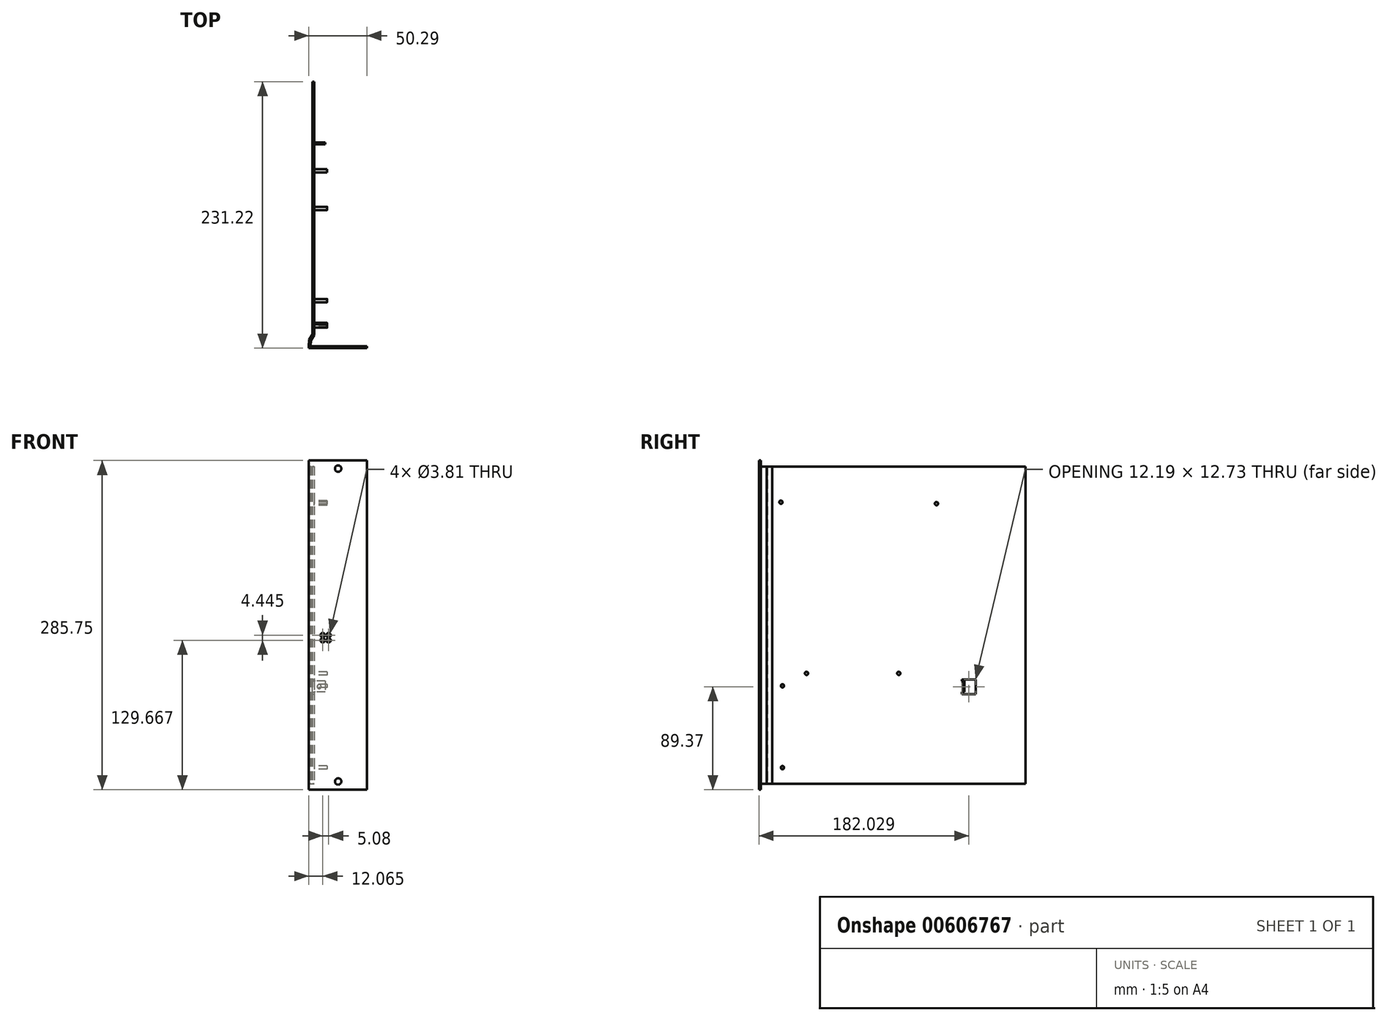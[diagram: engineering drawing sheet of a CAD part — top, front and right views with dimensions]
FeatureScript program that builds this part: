
annotation { "Feature Type Name" : "Feature", "Feature Type Description" : "" }
export const myFeature = defineFeature(function(context is Context, id is Id, definition is map)
    precondition{}
    {
        {
            var Q0;
            Q0=qCreatedBy(makeId("Top.planeOp"),FACE);
            var sketch = newSketch(context, id + "F0", { "sketchPlane" : qUnion([Q0])});
            skLineSegment(sketch, "E0", {"start": v(0, 0) * mm, "end": v(50.3, 0) * mm});
            skLineSegment(sketch, "E1", {"start": v(0, 0) * mm, "end": v(0, 1.6) * mm});
            skLineSegment(sketch, "E2.0", {"start": v(3.15, 231.22) * mm, "end": v(4.75, 231.22) * mm});
            skLineSegment(sketch, "E3.0", {"start": v(3.15, 11.84) * mm, "end": v(3.15, 231.22) * mm});
            skLineSegment(sketch, "E4.0", {"start": v(4.75, 11.38) * mm, "end": v(4.75, 231.22) * mm});
            skLineSegment(sketch, "E5.0", {"start": v(1.6, 1.6) * mm, "end": v(50.3, 1.6) * mm});
            skLineSegment(sketch, "E6", {"start": v(0, 1.6) * mm, "end": v(0.3, 7.25) * mm});
            skLineSegment(sketch, "E7", {"start": v(3.15, 11.84) * mm, "end": v(0.3, 7.25) * mm});
            skLineSegment(sketch, "E8.0", {"start": v(4.75, 11.38) * mm, "end": v(1.87, 6.76) * mm});
            skLineSegment(sketch, "E9.0", {"start": v(1.6, 1.6) * mm, "end": v(1.87, 6.76) * mm});
            skLineSegment(sketch, "E10", {"start": v(50.3, 1.6) * mm, "end": v(50.3, 0) * mm});
            skSolve(sketch);
        }
        {
            var Q0;
            Q0=qSketchRegion(id+"F0",true);
            extrude(context, id + "F1", {"entities" : qUnion([Q0]), "depth" : 285.75 * mm, "offsetDistance" : 25.4 * mm});
        }
        {
            var Q0;
            Q0=qCreatedBy(makeId("Right.planeOp"),FACE);
            var sketch = newSketch(context, id + "F2", { "sketchPlane" : qUnion([Q0])});
            skLineSegment(sketch, "E11.bottom", {"start": v(231.22, 0) * mm, "end": v(1.6, 0) * mm});
            skLineSegment(sketch, "E11.top", {"start": v(231.22, 5.08) * mm, "end": v(1.6, 5.08) * mm});
            skLineSegment(sketch, "E11.left", {"start": v(231.22, 0) * mm, "end": v(231.22, 5.08) * mm});
            skLineSegment(sketch, "E11.right", {"start": v(1.6, 0) * mm, "end": v(1.6, 5.08) * mm});
            skSolve(sketch);
        }
        {
            var Q0;
            Q0=makeQuery(id+"F2.imprint","IMPRINT",FACE,{"disambiguationData":[TD([[makeQuery(id+"F2.imprint","IMPRINT",EDGE,{"derivedFrom":sQuery(id+"F2.wireOp",EDGE,"E11.bottom")}),-1.0]])]});
            extrude(context, id + "F3", {"entities" : qUnion([Q0]), "operationType" : NewBodyOperationType.REMOVE, "depth" : 6.35 * mm, "offsetDistance" : 25.4 * mm});
        }
        {
            var Q0;
            Q0=qCreatedBy(makeId("Right.planeOp"),FACE);
            var sketch = newSketch(context, id + "F4", { "sketchPlane" : qUnion([Q0])});
            skLineSegment(sketch, "E12.bottom", {"start": v(231.22, 285.75) * mm, "end": v(1.6, 285.75) * mm});
            skLineSegment(sketch, "E12.top", {"start": v(231.22, 280.42) * mm, "end": v(1.6, 280.42) * mm});
            skLineSegment(sketch, "E12.left", {"start": v(231.22, 285.75) * mm, "end": v(231.22, 280.42) * mm});
            skLineSegment(sketch, "E12.right", {"start": v(1.6, 285.75) * mm, "end": v(1.6, 280.42) * mm});
            skSolve(sketch);
        }
        {
            var Q0;
            Q0=qSketchRegion(id+"F4",true);
            extrude(context, id + "F5", {"entities" : qUnion([Q0]), "operationType" : NewBodyOperationType.REMOVE, "depth" : 6.35 * mm, "offsetDistance" : 25.4 * mm});
        }
        {
            var Q0;
            Q0=makeQuery(id+"F1.opExtrude","SWEPT_FACE",FACE,{"disambiguationData":[OSD([sQuery(id+"F0.wireOp",EDGE,"E4.0")])]});
            var sketch = newSketch(context, id + "F6", { "sketchPlane" : qUnion([Q0])});
            skCircle(sketch, "E13", {"center": v(154, 248.28) * mm, "radius": 1.42 * mm});
            skCircle(sketch, "E14", {"center": v(19.13, 249.55) * mm, "radius": 1.42 * mm});
            skCircle(sketch, "E15", {"center": v(121.28, 100.96) * mm, "radius": 1.42 * mm});
            skCircle(sketch, "E16", {"center": v(20.42, 90.14) * mm, "radius": 1.42 * mm});
            skPoint(sketch, "E17", {"position": v(41.28, 100.96) * mm});
            skCircle(sketch, "E18", {"center": v(41.28, 100.96) * mm, "radius": 1.42 * mm});
            skPoint(sketch, "E19", {"position": v(20.42, 19.15) * mm});
            skCircle(sketch, "E20", {"center": v(20.42, 19.15) * mm, "radius": 1.42 * mm});
            skSolve(sketch);
        }
        {
            var Q0;
            Q0=qSketchRegion(id+"F6",true);
            extrude(context, id + "F7", {"entities" : qUnion([Q0]), "operationType" : NewBodyOperationType.ADD, "depth" : 11.1 * mm, "offsetDistance" : 25.4 * mm});
        }
        {
            var Q0;
            Q0=makeQuery(id+"F1.opExtrude","SWEPT_FACE",FACE,{"disambiguationData":[OSD([sQuery(id+"F0.wireOp",EDGE,"E4.0")])]});
            var sketch = newSketch(context, id + "F8", { "sketchPlane" : qUnion([Q0])});
            skLineSegment(sketch, "E21.bottom", {"start": v(175.93, 95.73) * mm, "end": v(188.13, 95.73) * mm});
            skLineSegment(sketch, "E21.top", {"start": v(175.93, 83) * mm, "end": v(188.13, 83) * mm});
            skLineSegment(sketch, "E21.left", {"start": v(175.93, 95.73) * mm, "end": v(175.93, 83) * mm});
            skLineSegment(sketch, "E21.right", {"start": v(188.13, 95.73) * mm, "end": v(188.13, 83) * mm});
            skSolve(sketch);
        }
        {
            var Q0;
            Q0=makeQuery(id+"F8.imprint","IMPRINT",FACE,{"disambiguationData":[TD([[makeQuery(id+"F8.imprint","IMPRINT",EDGE,{"derivedFrom":sQuery(id+"F8.wireOp",EDGE,"E21.bottom")}),-1.0]])]});
            extrude(context, id + "F9", {"entities" : qUnion([Q0]), "operationType" : NewBodyOperationType.REMOVE, "oppositeDirection" : true, "depth" : 25.4 * mm, "offsetDistance" : 25.4 * mm});
        }
        {
            var Q0;
            Q0=qCreatedBy(makeId("Top.planeOp"),FACE);
            cPlane(context, id + "F10", {"entities" : qUnion([Q0]), "cplaneType" : CPlaneType.OFFSET, "offset" : 84.73 * mm, "width" : 152.4 * mm, "height" : 152.4 * mm});
        }
        {
            var Q0;
            Q0=qCreatedBy(id+"F10.planeOp",FACE);
            var sketch = newSketch(context, id + "F11", { "sketchPlane" : qUnion([Q0])});
            skLineSegment(sketch, "E22.0", {"start": v(14.27, 178.33) * mm, "end": v(14.27, 176.73) * mm});
            skLineSegment(sketch, "E23", {"start": v(14.27, 176.73) * mm, "end": v(5.55, 176.73) * mm});
            skLineSegment(sketch, "E24.0", {"start": v(14.27, 178.33) * mm, "end": v(4.75, 178.33) * mm});
            skArc(sketch, "E25", {"start": v(5.55, 176.73) * mm, "mid": v(4.98, 176.5) * mm, "end": v(4.75, 175.93) * mm});
            skLineSegment(sketch, "E26", {"start": v(3.15, 175.93) * mm, "end": v(3.15, 176.73) * mm});
            skArc(sketch, "E27", {"start": v(4.75, 178.33) * mm, "mid": v(3.62, 177.86) * mm, "end": v(3.15, 176.73) * mm});
            skLineSegment(sketch, "E28.0", {"start": v(3.15, 175.93) * mm, "end": v(4.75, 175.93) * mm});
            skSolve(sketch);
        }
        {
            var Q0;
            Q0=makeQuery(id+"F11.imprint","IMPRINT",FACE,{"disambiguationData":[TD([[makeQuery(id+"F11.imprint","IMPRINT",EDGE,{"derivedFrom":sQuery(id+"F11.wireOp",EDGE,"E22.0")}),-1.0]])]});
            extrude(context, id + "F12", {"entities" : qUnion([Q0]), "operationType" : NewBodyOperationType.ADD, "depth" : 9.52 * mm, "offsetDistance" : 25.4 * mm});
        }
        {
            var Q0;
            Q0=makeQuery(id+"F12.opExtrude","SWEPT_FACE",FACE,{"disambiguationData":[OSD([sQuery(id+"F11.wireOp",EDGE,"E24.0")])]});
            var sketch = newSketch(context, id + "F13", { "sketchPlane" : qUnion([Q0])});
            skCircle(sketch, "E29", {"center": v(-9, 89.5) * mm, "radius": 1.78 * mm});
            skPoint(sketch, "E29.centerSnap0", {"position": v(-14.27, 89.5) * mm});
            skSolve(sketch);
        }
        {
            var Q0;
            Q0=makeQuery(id+"F13.imprint","IMPRINT",FACE,{"disambiguationData":[TD([[makeQuery(id+"F13.imprint","IMPRINT",EDGE,{"derivedFrom":sQuery(id+"F13.wireOp",EDGE,"E29")}),1.0]])]});
            extrude(context, id + "F14", {"entities" : qUnion([Q0]), "operationType" : NewBodyOperationType.REMOVE, "endBound" : BoundingType.UP_TO_NEXT, "oppositeDirection" : true, "depth" : 25.4 * mm, "offsetDistance" : 25.4 * mm});
        }
        {
            var Q0;
            Q0=makeQuery(id+"F1.opExtrude","SWEPT_FACE",FACE,{"disambiguationData":[OSD([sQuery(id+"F0.wireOp",EDGE,"E0")])]});
            var sketch = newSketch(context, id + "F15", { "sketchPlane" : qUnion([Q0])});
            skCircle(sketch, "E30", {"center": v(12.07, 134.11) * mm, "radius": 1.9 * mm});
            skCircle(sketch, "E31", {"center": v(17.14, 134.11) * mm, "radius": 1.9 * mm});
            skCircle(sketch, "E32", {"center": v(12.07, 129.67) * mm, "radius": 1.9 * mm});
            skCircle(sketch, "E33", {"center": v(17.14, 129.67) * mm, "radius": 1.9 * mm});
            skSolve(sketch);
        }
        {
            var Q0;
            Q0 = qSketchRegion(id + "F15", true);
            extrude(context, id + "F16", {"entities" : qUnion([Q0]), "operationType" : NewBodyOperationType.REMOVE, "endBound" : BoundingType.UP_TO_NEXT, "oppositeDirection" : true, "depth" : 25.4 * mm, "offsetDistance" : 25.4 * mm});
        }
        {
            var Q0;
            Q0=makeQuery(id+"F1.opExtrude","SWEPT_FACE",FACE,{"disambiguationData":[OSD([sQuery(id+"F0.wireOp",EDGE,"E0")])]});
            var sketch = newSketch(context, id + "F17", { "sketchPlane" : qUnion([Q0])});
            skCircle(sketch, "E34", {"center": v(25.43, 7.11) * mm, "radius": 2.78 * mm});
            skCircle(sketch, "E35", {"center": v(25.43, 278.64) * mm, "radius": 2.78 * mm});
            skSolve(sketch);
        }
        {
            var Q0;
            Q0 = qSketchRegion(id + "F17", true);
            extrude(context, id + "F18", {"entities" : qUnion([Q0]), "operationType" : NewBodyOperationType.REMOVE, "endBound" : BoundingType.UP_TO_NEXT, "oppositeDirection" : true, "depth" : 25.4 * mm, "offsetDistance" : 25.4 * mm});
        }
    });
